# Revit family: PractiboxS flush cabinet for masonry wall
name_source: partatom
category: Equipement spécialisé
units: mm (PartAtom-declared; Revit-internal decimal feet)

## family parameters
Basée sur le plan de construction = Non
Cote de connecteur circulaire = Utiliser le diamètre
Couper avec des vides une fois chargée = Non
Numéro OmniClass = 23.80.30.11.17
Partagée = Oui
Point de calcul de pièce = Non
Titre OmniClass = Distribution Boards and Control Panels
Toujours verticalement = Oui
Type d'élément = Normal

## types (1)
- Communication board 135722
    BIM wording = Communication board 135722
    Color = White
    Depth (mm) = 103 mm  [stored 0.337927 ft]
    E-catalogue link = https://www.legrand.fr
    EAN = 3414972144278
    ETIM class = EC003845
    Elévation par défaut = 0 mm  [stored 0 ft]
    Fabricant = LEGRAND
    Function = Communication board
    General Conditions of Use = https://export.legrand.com
    Height (mm) = 328 mm  [stored 1.07612 ft]
    Legrand part number = 135722
    RAL Number = 9003
    Type of door = With door
    Width (mm) = 18 mm  [stored 0.0590551 ft]

note: [stored X ft] marks values corroborated as IEEE doubles in the binary element streams (Revit-internal decimal feet)
